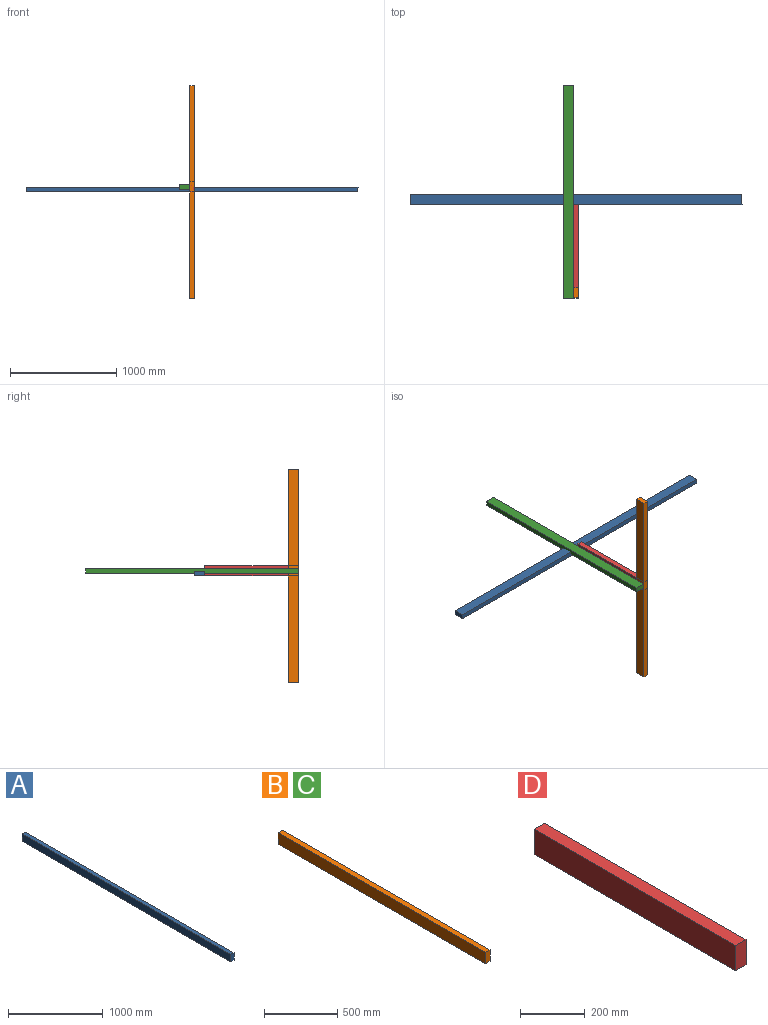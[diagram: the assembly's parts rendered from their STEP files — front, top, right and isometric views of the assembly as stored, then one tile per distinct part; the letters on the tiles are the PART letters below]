
ASSEMBLY  parts=4 mates=3
PART A: 6 faces, bbox 45x3125x95 mm
  f0: plane 3125x95mm, normal (-1,0,0), area 296875mm2, adj f1,f3,f4,f5
  f1: plane 3125x45mm, normal (0,0,-1), area 140625mm2, adj f0,f2,f4,f5
  f2: plane 3125x95mm, normal (1,0,0), area 296875mm2, adj f1,f3,f4,f5
  f3: plane 3125x45mm, normal (0,0,1), area 140625mm2, adj f0,f2,f4,f5
  f4: plane 95x45mm, normal (0,-1,0), area 4275mm2, adj f0,f1,f2,f3
  f5: plane 95x45mm, normal (0,1,0), area 4275mm2, adj f0,f1,f2,f3
PART B: 6 faces, bbox 45x2000x95 mm
  f0: plane 2000x95mm, normal (-1,0,0), area 190000mm2, adj f1,f3,f4,f5
  f1: plane 2000x45mm, normal (0,0,-1), area 90000mm2, adj f0,f2,f4,f5
  f2: plane 2000x95mm, normal (1,0,0), area 190000mm2, adj f1,f3,f4,f5
  f3: plane 2000x45mm, normal (0,0,1), area 90000mm2, adj f0,f2,f4,f5
  f4: plane 95x45mm, normal (0,-1,0), area 4275mm2, adj f0,f1,f2,f3
  f5: plane 95x45mm, normal (0,1,0), area 4275mm2, adj f0,f1,f2,f3
PART C: same geometry as B
PART D: 6 faces, bbox 45x880x95 mm
  f0: plane 880x95mm, normal (-1,0,0), area 83600mm2, adj f1,f3,f4,f5
  f1: plane 880x45mm, normal (0,0,-1), area 39600mm2, adj f0,f2,f4,f5
  f2: plane 880x95mm, normal (1,0,0), area 83600mm2, adj f1,f3,f4,f5
  f3: plane 880x45mm, normal (0,0,1), area 39600mm2, adj f0,f2,f4,f5
  f4: plane 95x45mm, normal (0,-1,0), area 4275mm2, adj f0,f1,f2,f3
  f5: plane 95x45mm, normal (0,1,0), area 4275mm2, adj f0,f1,f2,f3
PLACE A rot(axis=(0.58,-0.58,0.58),120deg) t=(-2011.25,-3.86,-306.35)mm
PLACE B rot(axis=(-1,0,0),90deg) t=(-471.25,-978.86,-1306.35)mm
PLACE C rot(axis=(0,-1,0),90deg) t=(-471.25,1021.14,-281.35)mm
PLACE D rot(axis=(-1,0,0),180deg) t=(-471.25,-978.86,-211.35)mm
MATE fastened D.f4 <-> A.f3  axis (0,1,0) through (-448.75,-98.86,-306.35)mm
MATE planar B.f1 <-> D.f5  axis (0,-1,0) through (-448.75,-978.86,-306.35)mm
MATE planar C.f1 <-> D.f0  axis (1,0,0) through (-471.25,-978.86,-258.85)mm
